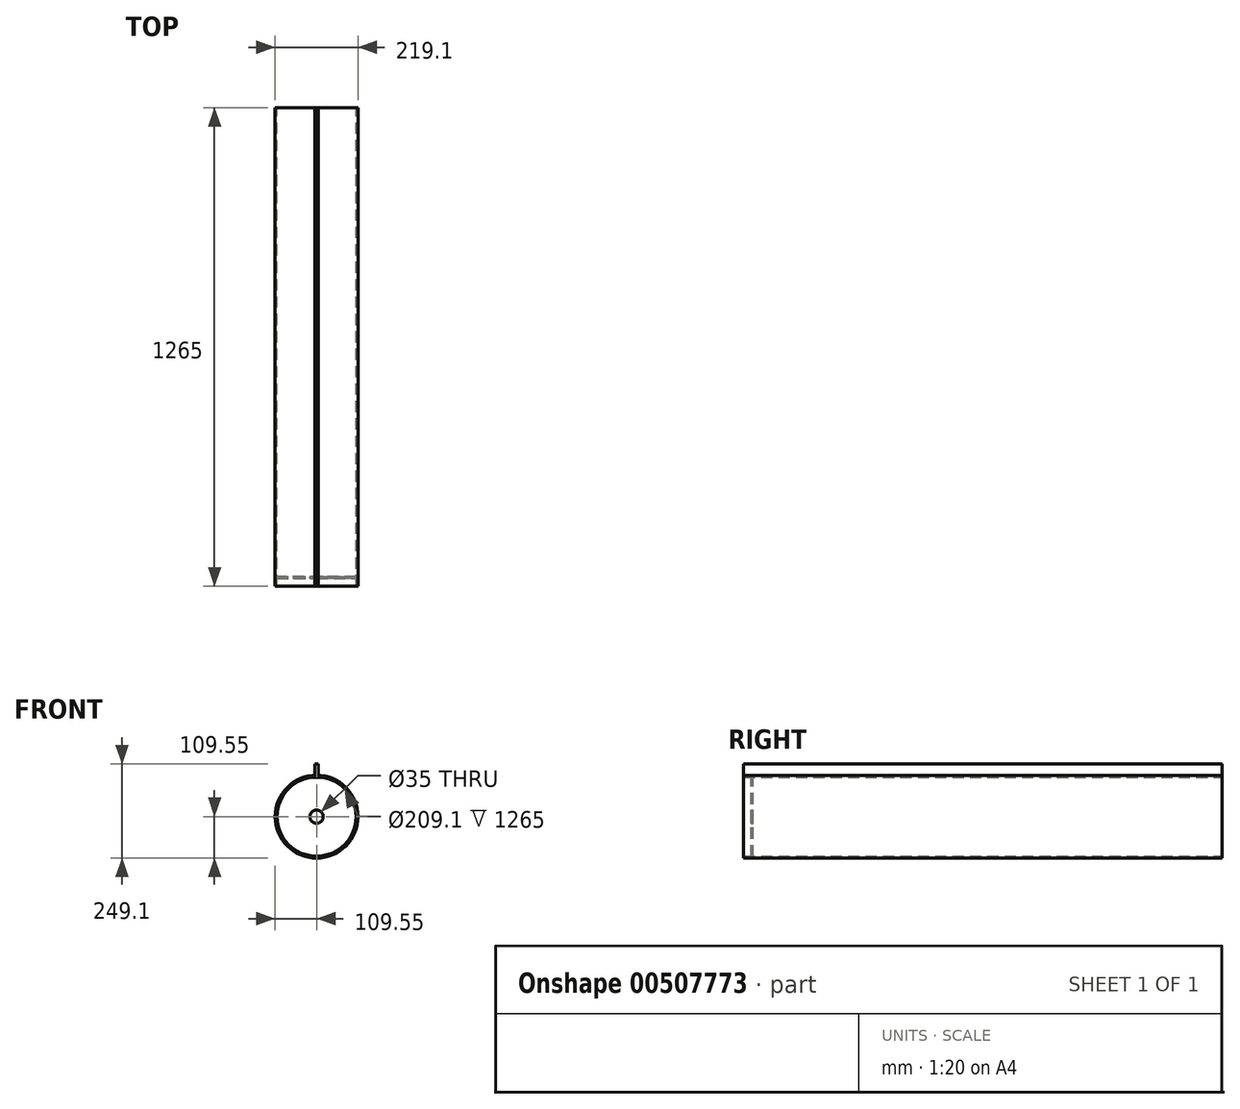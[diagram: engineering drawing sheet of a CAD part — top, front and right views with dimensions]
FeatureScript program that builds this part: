
annotation { "Feature Type Name" : "Feature", "Feature Type Description" : "" }
export const myFeature = defineFeature(function(context is Context, id is Id, definition is map)
    precondition{}
    {
        {
            assignVariable(context, id + "F0", {"name" : "L", "anyValue" : 1265});
        }
        {
            var Q0;
            Q0=qCreatedBy(makeId("Front.planeOp"),FACE);
            var sketch = newSketch(context, id + "F1", { "sketchPlane" : qUnion([Q0])});
            skCircle(sketch, "E0", {"center": v(0, 0) * mm, "radius": 17.5 * mm});
            skCircle(sketch, "E1", {"center": v(0, 0) * mm, "radius": 109.55 * mm});
            skCircle(sketch, "E2.0", {"center": v(0, 0) * mm, "radius": 104.55 * mm});
            skLineSegment(sketch, "E3.bottom", {"start": v(-5, 139.55) * mm, "end": v(5, 139.55) * mm});
            skLineSegment(sketch, "E3.top", {"start": v(-5, 109.55) * mm, "end": v(5, 109.55) * mm});
            skLineSegment(sketch, "E3.left", {"start": v(-5, 139.55) * mm, "end": v(-5, 109.55) * mm});
            skLineSegment(sketch, "E3.right", {"start": v(5, 139.55) * mm, "end": v(5, 109.55) * mm});
            skPoint(sketch, "E3.middle", {"position": v(0, 124.55) * mm});
            skSolve(sketch);
        }
        {
            var Q0;
            Q0=makeQuery(id+"F1.imprint","IMPRINT",FACE,{"disambiguationData":[TD([[makeQuery(id+"F1.imprint","IMPRINT",EDGE,{"derivedFrom":sQuery(id+"F1.wireOp",EDGE,"E1")}),1.0]])]});
            extrude(context, id + "F2", {"entities" : qUnion([Q0]), "endBound" : BoundingType.SYMMETRIC, "depth" : (getVariable(context, 'L')) * mm, "hasSecondDirection" : true, "secondDirectionOppositeDirection" : true, "secondDirectionDepth" : 25 * mm});
        }
        {
            var Q0;
            Q0=makeQuery(id+"F1.imprint","IMPRINT",FACE,{"disambiguationData":[TD([[makeQuery(id+"F1.imprint","IMPRINT",EDGE,{"derivedFrom":sQuery(id+"F1.wireOp",EDGE,"E0")}),-1.0]])]});
            extrude(context, id + "F3", {"entities" : qUnion([Q0]), "depth" : (getVariable(context, 'L') / 2 - 20) * mm, "hasSecondDirection" : true, "secondDirectionOppositeDirection" : false, "secondDirectionDepth" : (getVariable(context, 'L') / 2 - 25) * mm});
        }
        {
            var Q0;
            Q0=makeQuery(id+"F1.imprint","IMPRINT",FACE,{"disambiguationData":[TD([[makeQuery(id+"F1.imprint","IMPRINT",EDGE,{"derivedFrom":sQuery(id+"F1.wireOp",EDGE,"E3.bottom")}),-1.0]])]});
            var Q1;
            Q1=makeQuery(id+"F2.opExtrude","CAP_FACE",FACE,{"disambiguationData":[OSD([sQuery(id+"F1.wireOp",EDGE,"E1"),sQuery(id+"F1.wireOp",EDGE,"E2.0")])],"isStart":false});
            var Q2;
            Q2=makeQuery(id+"F2.opExtrude","CAP_FACE",FACE,{"disambiguationData":[OSD([sQuery(id+"F1.wireOp",EDGE,"E1"),sQuery(id+"F1.wireOp",EDGE,"E2.0")])],"isStart":true});
            extrude(context, id + "F4", {"entities" : qUnion([Q0]), "endBound" : BoundingType.UP_TO_SURFACE, "endBoundEntityFace" : qUnion([Q1]), "depth" : 1500 * mm, "hasSecondDirection" : true, "secondDirectionBound" : SecondDirectionBoundingType.UP_TO_SURFACE, "secondDirectionOppositeDirection" : true, "secondDirectionBoundEntityFace" : qUnion([Q2]), "secondDirectionDepth" : 25 * mm});
        }
    });
